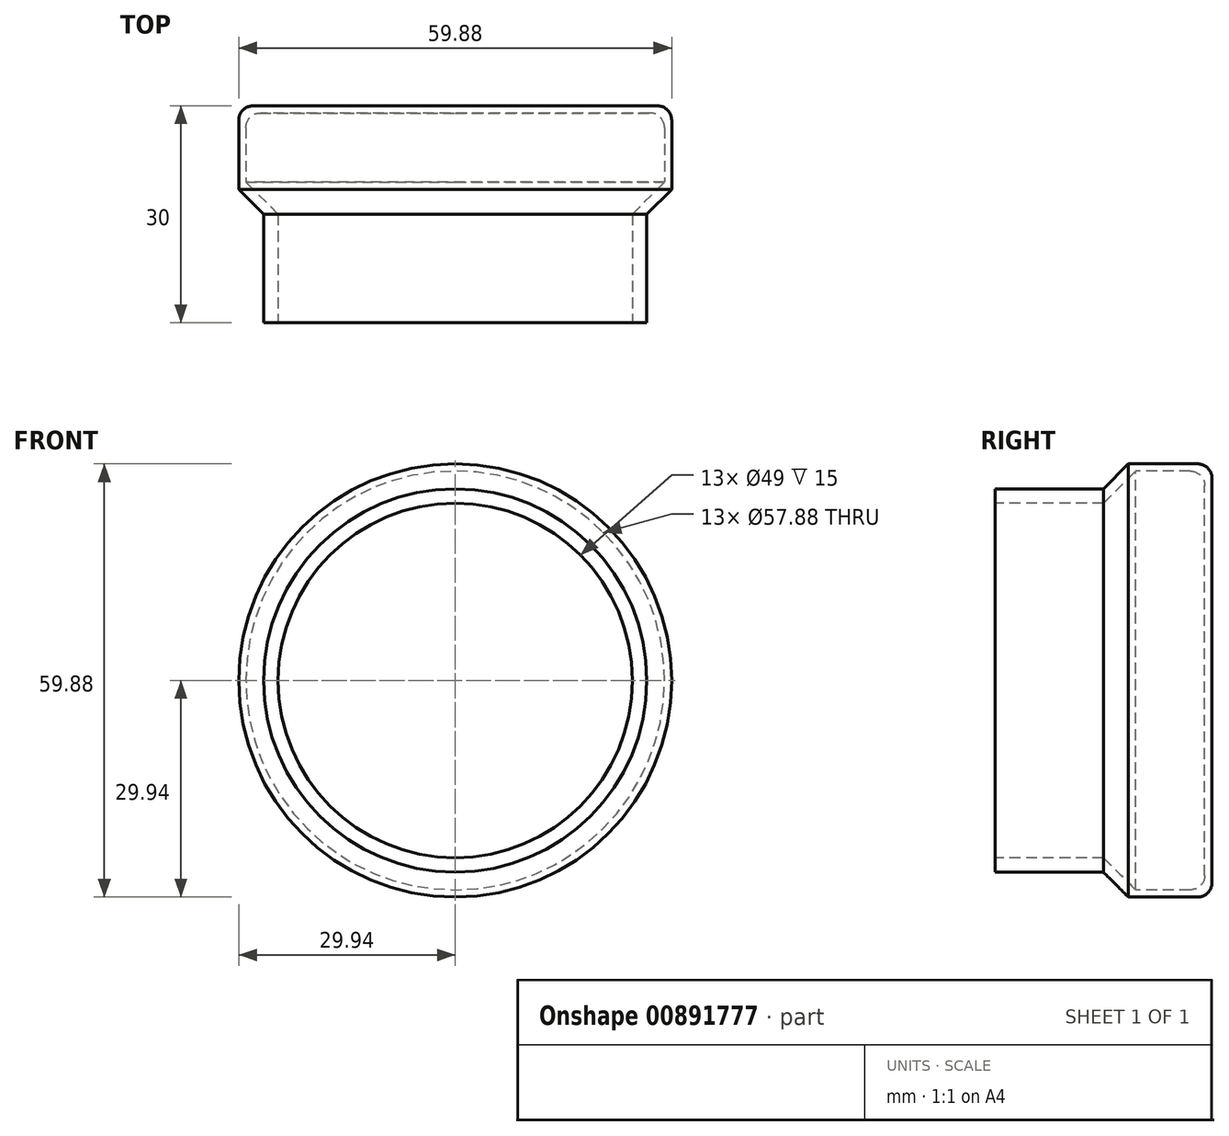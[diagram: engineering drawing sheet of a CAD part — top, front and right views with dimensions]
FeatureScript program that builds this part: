
annotation { "Feature Type Name" : "Feature", "Feature Type Description" : "" }
export const myFeature = defineFeature(function(context is Context, id is Id, definition is map)
    precondition{}
    {
        {
            var Q0;
            Q0=qCreatedBy(makeId("Right.planeOp"),FACE);
            var sketch = newSketch(context, id + "F0", { "sketchPlane" : qUnion([Q0])});
            skLineSegment(sketch, "E0.bottom", {"start": v(0, 0) * mm, "end": v(15, 0) * mm});
            skLineSegment(sketch, "E0.top", {"start": v(0, 26.5) * mm, "end": v(15, 26.5) * mm});
            skLineSegment(sketch, "E0.left", {"start": v(0, 0) * mm, "end": v(0, 26.5) * mm});
            skLineSegment(sketch, "E0.right", {"start": v(15, 0) * mm, "end": v(15, 26.5) * mm});
            skLineSegment(sketch, "E1.bottom", {"start": v(15, 29.94) * mm, "end": v(28, 29.94) * mm});
            skLineSegment(sketch, "E1.top", {"start": v(15, 0) * mm, "end": v(30, 0) * mm});
            skLineSegment(sketch, "E1.left", {"start": v(15, 29.94) * mm, "end": v(15, 0) * mm});
            skLineSegment(sketch, "E1.right", {"start": v(30, 27.94) * mm, "end": v(30, 0) * mm});
            skPoint(sketch, "E2.visualSharp", {"position": v(30, 29.94) * mm});
            skArc(sketch, "E2.filletArc", {"start": v(30, 27.94) * mm, "mid": v(29.41, 29.35) * mm, "end": v(28, 29.94) * mm});
            skLineSegment(sketch, "E3", {"start": v(15, 26.5) * mm, "end": v(18.44, 29.94) * mm});
            skLineSegment(sketch, "E4.top", {"start": v(0, 24.5) * mm, "end": v(15, 24.5) * mm});
            skLineSegment(sketch, "E4.left", {"start": v(0, 0) * mm, "end": v(0, 24.5) * mm});
            skLineSegment(sketch, "E4.right", {"start": v(15, 0) * mm, "end": v(15, 24.5) * mm});
            skLineSegment(sketch, "E5", {"start": v(15, 24.5) * mm, "end": v(20.44, 29.94) * mm});
            skLineSegment(sketch, "E6.0", {"start": v(15, 28.94) * mm, "end": v(27, 28.94) * mm});
            skLineSegment(sketch, "E7.0", {"start": v(29, 26.94) * mm, "end": v(29, 0) * mm});
            skPoint(sketch, "E8.visualSharp", {"position": v(29, 28.94) * mm});
            skArc(sketch, "E8.filletArc", {"start": v(29, 26.94) * mm, "mid": v(28.41, 28.35) * mm, "end": v(27, 28.94) * mm});
            skSolve(sketch);
        }
        {
            var Q0;
            {var subQ0=sQuery(id+"F0.wireOp",EDGE,"E0.top");Q0=makeQuery(id+"F0.imprint","IMPRINT",FACE,{"disambiguationData":[TD([[makeQuery(id+"F0.imprint","IMPRINT",EDGE,{"derivedFrom":subQ0}),-1.0]])]});}
            var Q1;
            {var subQ0=sQuery(id+"F0.wireOp",EDGE,"E3");var subQ5=sQuery(id+"F0.wireOp",EDGE,"E6.0");var subQ6=makeQuery(id+"F0.imprint","INTERSECT",VERTEX,{"derivedFrom":[subQ0,subQ5]});Q1=makeQuery(id+"F0.imprint","IMPRINT",FACE,{"disambiguationData":[TD([[makeQuery(id+"F0.imprint","IMPRINT",EDGE,{"disambiguationData":[TD([[subQ6,-1.0]])],"derivedFrom":subQ5}),-1.0]])]});}
            var Q2;
            {var subQ0=sQuery(id+"F0.wireOp",EDGE,"E3");var subQ1=sQuery(id+"F0.wireOp",EDGE,"E1.bottom");var subQ2=makeQuery(id+"F0.imprint","INTERSECT",VERTEX,{"derivedFrom":[subQ1,subQ0]});Q2=makeQuery(id+"F0.imprint","IMPRINT",FACE,{"disambiguationData":[TD([[makeQuery(id+"F0.imprint","IMPRINT",EDGE,{"disambiguationData":[TD([[subQ2,-1.0]])],"derivedFrom":subQ1}),-1.0]])]});}
            var Q3;
            {var subQ0=sQuery(id+"F0.wireOp",EDGE,"E1.right");Q3=makeQuery(id+"F0.imprint","IMPRINT",FACE,{"disambiguationData":[TD([[makeQuery(id+"F0.imprint","IMPRINT",EDGE,{"derivedFrom":subQ0}),-1.0]])]});}
            var Q4;
            Q4=sQuery(id+"F0.wireOp",EDGE,"E0.bottom");
            revolve(context, id + "F1", {"surfaceOperationType" : NewSurfaceOperationType.NEW, "entities" : qUnion([Q0, Q1, Q2, Q3]), "axis" : qUnion([Q4]), "revolveType" : RevolveType.FULL});
        }
    });
